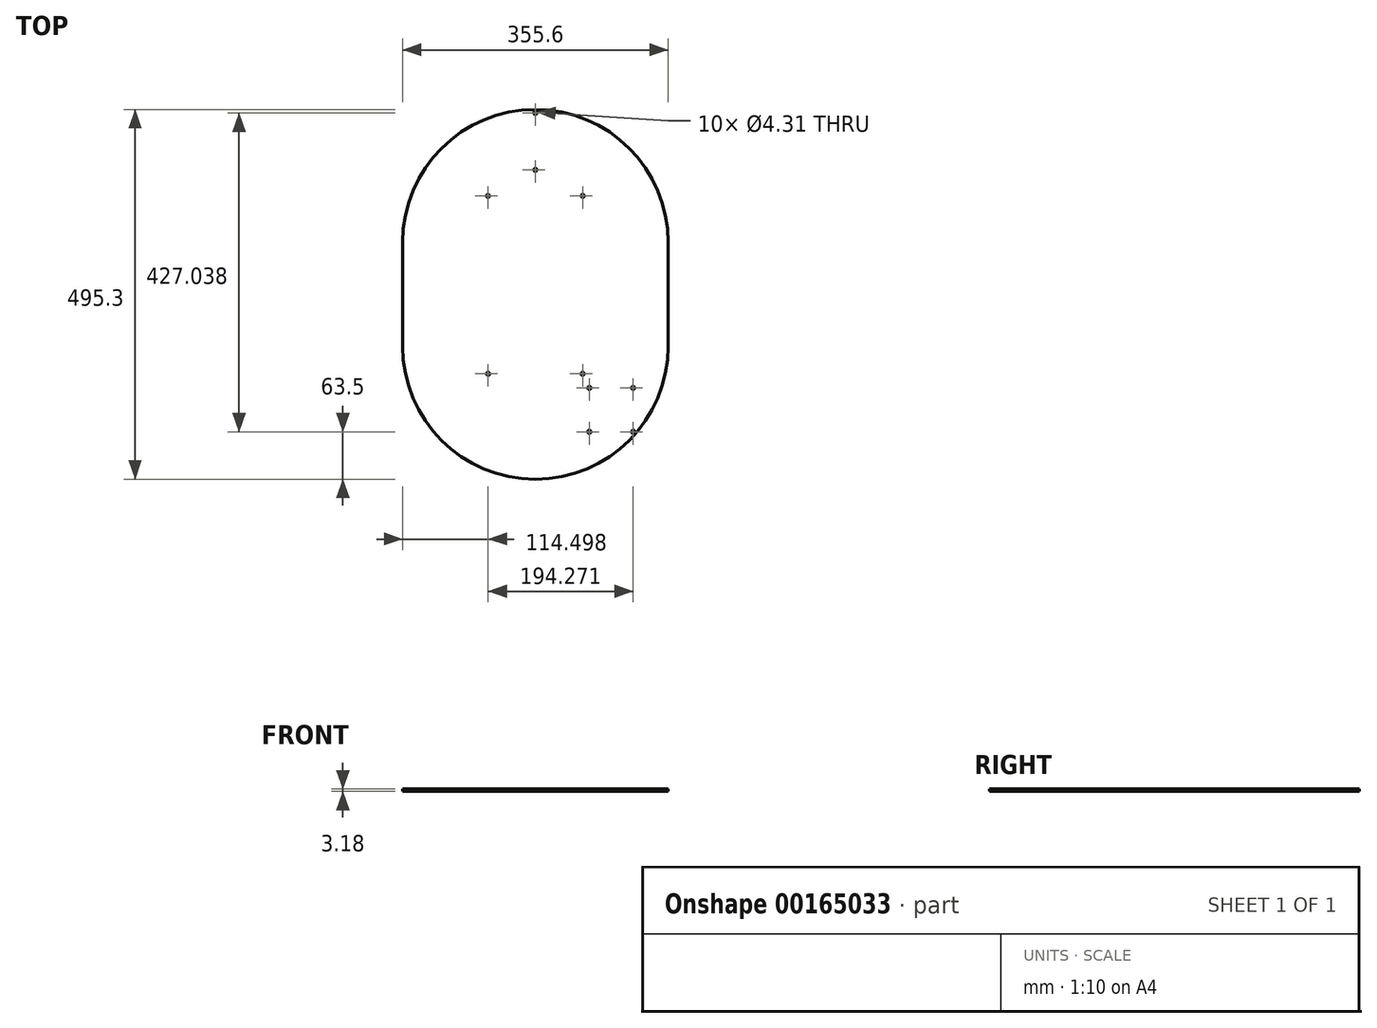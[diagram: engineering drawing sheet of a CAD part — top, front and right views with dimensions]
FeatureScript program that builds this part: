
annotation { "Feature Type Name" : "Feature", "Feature Type Description" : "" }
export const myFeature = defineFeature(function(context is Context, id is Id, definition is map)
    precondition{}
    {
        {
            var Q0;
            Q0=qCreatedBy(makeId("Top.planeOp"),FACE);
            var sketch = newSketch(context, id + "F0", { "sketchPlane" : qUnion([Q0])});
            skLineSegment(sketch, "E0.top", {"start": v(0, -139.7) * mm, "end": v(355.6, -139.7) * mm, "construction": true});
            skLineSegment(sketch, "E0.left", {"start": v(0, 0) * mm, "end": v(0, -139.7) * mm});
            skLineSegment(sketch, "E0.right", {"start": v(355.6, 0) * mm, "end": v(355.6, -139.7) * mm});
            skArc(sketch, "E1", {"start": v(0, -139.7) * mm, "mid": v(177.8, -317.5) * mm, "end": v(355.6, -139.7) * mm});
            skLineSegment(sketch, "E2", {"start": v(177.8, -57.15) * mm, "end": v(177.8, -176.32) * mm, "construction": true});
            skLineSegment(sketch, "E3", {"start": v(177.8, -57.15) * mm, "end": v(177.8, 62.02) * mm, "construction": true});
            skLineSegment(sketch, "E4", {"start": v(114.5, 62.02) * mm, "end": v(241.1, 62.02) * mm, "construction": true});
            skLineSegment(sketch, "E5", {"start": v(241.1, 62.02) * mm, "end": v(177.8, -57.15) * mm, "construction": true});
            skLineSegment(sketch, "E6", {"start": v(177.8, -57.15) * mm, "end": v(114.5, 62.02) * mm, "construction": true});
            skLineSegment(sketch, "E7", {"start": v(114.5, -176.32) * mm, "end": v(241.1, -176.32) * mm, "construction": true});
            skLineSegment(sketch, "E8", {"start": v(177.8, -176.32) * mm, "end": v(177.8, -224.63) * mm, "construction": true});
            skLineSegment(sketch, "E9", {"start": v(177.8, -224.63) * mm, "end": v(279.4, -224.63) * mm, "construction": true});
            skLineSegment(sketch, "E10.bottom", {"start": v(308.77, -195.26) * mm, "end": v(250.03, -195.26) * mm, "construction": true});
            skLineSegment(sketch, "E10.top", {"start": v(308.77, -254) * mm, "end": v(250.03, -254) * mm, "construction": true});
            skLineSegment(sketch, "E10.left", {"start": v(308.77, -195.26) * mm, "end": v(308.77, -254) * mm, "construction": true});
            skLineSegment(sketch, "E10.right", {"start": v(250.03, -195.26) * mm, "end": v(250.03, -254) * mm, "construction": true});
            skPoint(sketch, "E10.middle", {"position": v(279.4, -224.63) * mm});
            skCircle(sketch, "E11", {"center": v(250.03, -195.26) * mm, "radius": 2.15 * mm});
            skCircle(sketch, "E12", {"center": v(250.03, -254) * mm, "radius": 2.15 * mm});
            skCircle(sketch, "E13", {"center": v(308.77, -254) * mm, "radius": 2.15 * mm});
            skCircle(sketch, "E14", {"center": v(308.77, -195.26) * mm, "radius": 2.15 * mm});
            skCircle(sketch, "E15", {"center": v(114.5, -176.32) * mm, "radius": 2.15 * mm});
            skCircle(sketch, "E16", {"center": v(241.1, -176.32) * mm, "radius": 2.15 * mm});
            skCircle(sketch, "E17", {"center": v(241.1, 62.02) * mm, "radius": 2.15 * mm});
            skCircle(sketch, "E18", {"center": v(114.5, 62.02) * mm, "radius": 2.15 * mm});
            skLineSegment(sketch, "E19", {"start": v(0, 0) * mm, "end": v(118.53, 0) * mm, "construction": true});
            skLineSegment(sketch, "E20", {"start": v(118.53, 0) * mm, "end": v(118.53, -57.15) * mm, "construction": true});
            skLineSegment(sketch, "E21", {"start": v(118.53, -57.15) * mm, "end": v(237.07, -57.15) * mm, "construction": true});
            skLineSegment(sketch, "E22", {"start": v(237.07, -57.15) * mm, "end": v(237.07, 0) * mm, "construction": true});
            skLineSegment(sketch, "E23", {"start": v(237.07, 0) * mm, "end": v(355.6, 0) * mm, "construction": true});
            skArc(sketch, "E24", {"start": v(355.6, 0) * mm, "mid": v(177.8, 177.8) * mm, "end": v(0, 0) * mm});
            skLineSegment(sketch, "E25", {"start": v(177.8, 177.8) * mm, "end": v(177.8, 173.04) * mm, "construction": true});
            skLineSegment(sketch, "E26", {"start": v(177.8, 173.04) * mm, "end": v(177.8, 96.84) * mm, "construction": true});
            skCircle(sketch, "E27", {"center": v(177.8, 173.04) * mm, "radius": 2.15 * mm});
            skCircle(sketch, "E28", {"center": v(177.8, 96.84) * mm, "radius": 2.15 * mm});
            skArc(sketch, "E29", {"start": v(241.1, 62.02) * mm, "mid": v(177.8, 77.79) * mm, "end": v(114.5, 62.02) * mm, "construction": true});
            skLineSegment(sketch, "E30", {"start": v(177.8, 96.84) * mm, "end": v(177.8, 77.79) * mm, "construction": true});
            skCircle(sketch, "E31", {"center": v(308.77, -254) * mm, "radius": 3.97 * mm, "construction": true});
            skSolve(sketch);
        }
        {
            var Q0;
            Q0=qSketchRegion(id+"F0",true);
            extrude(context, id + "F1", {"entities" : qUnion([Q0]), "depth" : 3.17 * mm});
        }
    });
